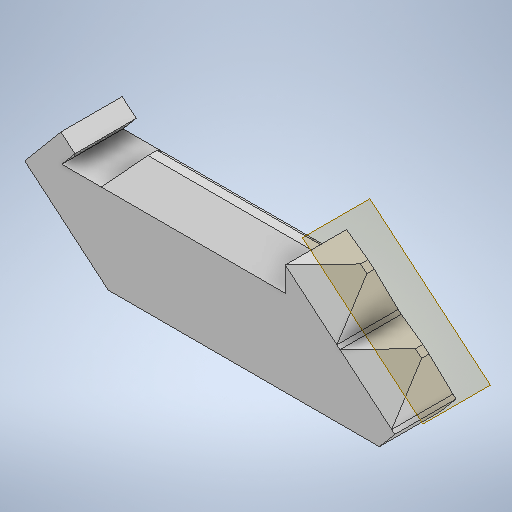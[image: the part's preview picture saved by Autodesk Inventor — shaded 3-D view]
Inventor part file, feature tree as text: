
AUTODESK INVENTOR PART (.ipt)
format: ipt  version: 2025 (Build 290162010, 162A)  size: 318,464 bytes
history: native  units: mm
features: sketch x8, extrude x3, projected_geometry x3, loft x2, plane x1
ambient origin geometry x8: Origin, YZ Plane, XZ Plane, XY Plane, X Axis, Y Axis, Z Axis, Center Point
bodies: Solid1 (feature_tree)
feature tree (17):
  extrude  "Extrusion1"  Depth=22.68928mm
  sketch  "Sketch2"  dims[d21=3500.0mm d22=90.0deg]
  plane  "Work Plane1"
  loft  "Loft1"
  loft  "Loft2"
  extrude  "Extrusion2"  TaperAngle=90.0deg  [1 undecoded]
  sketch  "Sketch7"  dims[d35=90.0deg]
  extrude  "Extrusion3"  Depth=8.726646mm
  sketch  "Sketch1"  dims[d19=587.0mm d20=22.68928mm]
  projected_geometry  "Projected Loop1"
  sketch  "Sketch3"  dims[d28=600.0mm d29=8.726646mm]
  sketch  "Sketch4"  dims[d30=5468.0mm d31=90.0deg]
  projected_geometry  "Projected Loop2"
  sketch  "Sketch5"  dims[d32=500.0mm d33=8.726646mm]
  sketch  "Sketch6"  dims[d34=450.0mm]
  sketch  "Sketch8"  dims[d36=1377.0mm d37=90.0deg d38=2671.0mm d39=90.0deg d40=6634.212065mm d41=24.43461mm d42=1500.0mm d43=0.0mm d44=1650.0mm d45=1500.0mm d46=100.0mm d47=980.0mm d48=182.0mm d49=200.0mm d50=0.0mm d51=90.0deg d52=0.0mm d53=90.0deg d54=1650.0mm d55=1500.0mm d56=100.0mm d59=200.0mm d60=182.0mm d61=0.0mm d62=90.0deg d63=0.0mm d64=90.0deg d65=220.0mm d67=4500.0mm d68=0.0mm d69=781.0mm d70=0.0mm d71=0.0mm]
  projected_geometry  "Projected Loop3"
note: 1 required parameter value undecoded (feature->parameter linkage not recoverable at this tier; creation-order binding heuristic only, values carry confidence <= 0.55)
